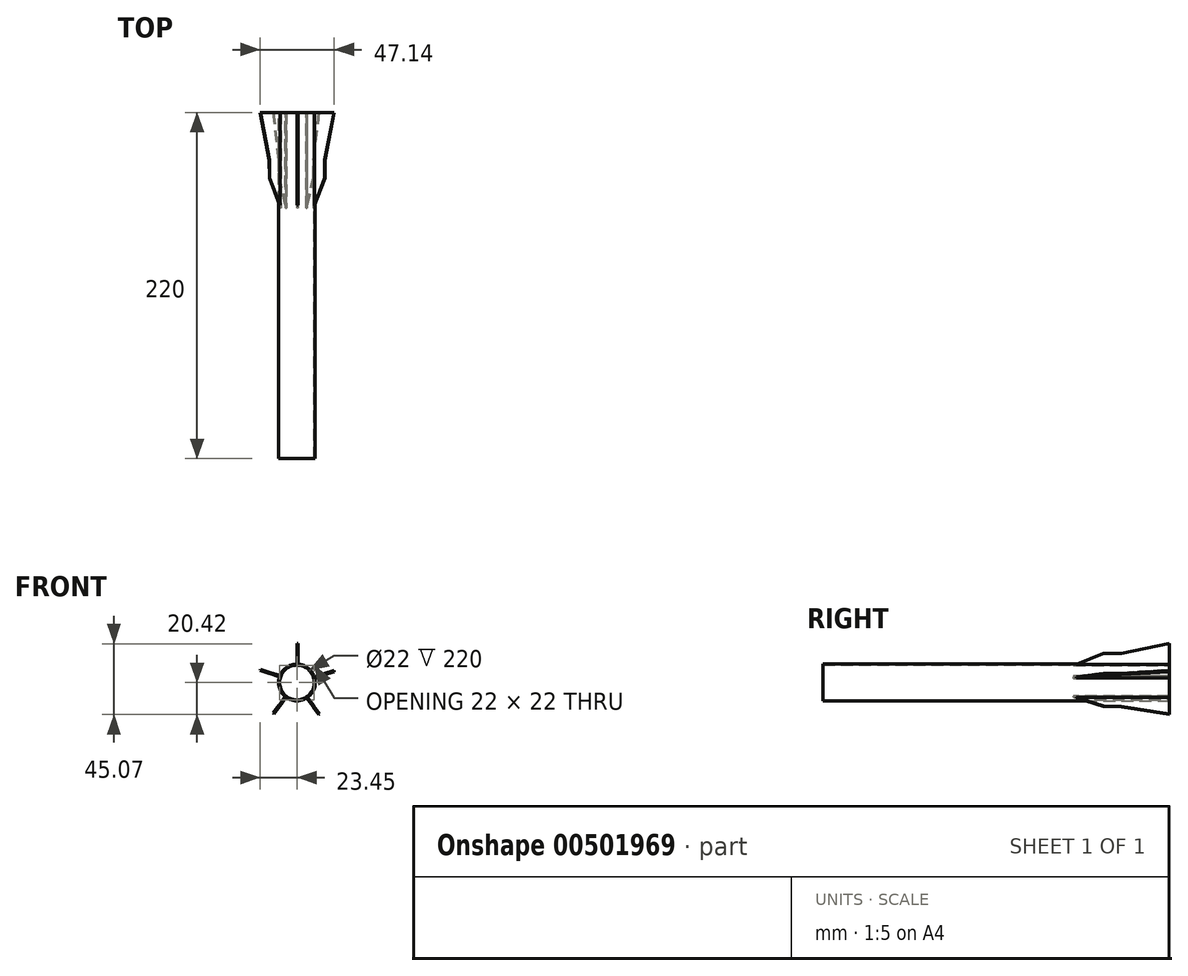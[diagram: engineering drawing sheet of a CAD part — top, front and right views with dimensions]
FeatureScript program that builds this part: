
annotation { "Feature Type Name" : "Feature", "Feature Type Description" : "" }
export const myFeature = defineFeature(function(context is Context, id is Id, definition is map)
    precondition{}
    {
        {
            var Q0;
            Q0=qCreatedBy(makeId("Front.planeOp"),FACE);
            var sketch = newSketch(context, id + "F0", { "sketchPlane" : qUnion([Q0])});
            skCircle(sketch, "E0", {"center": v(0, 0) * mm, "radius": 11 * mm});
            skCircle(sketch, "E1", {"center": v(0, 0) * mm, "radius": 11.65 * mm});
            skSolve(sketch);
        }
        {
            var Q0;
            Q0=makeQuery(id+"F0.imprint","IMPRINT",FACE,{"disambiguationData":[TD([[makeQuery(id+"F0.imprint","IMPRINT",EDGE,{"derivedFrom":sQuery(id+"F0.wireOp",EDGE,"E0")}),-1.0]])]});
            extrude(context, id + "F1", {"entities" : qUnion([Q0]), "depth" : 220 * mm});
        }
        {
            var Q0;
            Q0=qCreatedBy(makeId("Right.planeOp"),FACE);
            var sketch = newSketch(context, id + "F2", { "sketchPlane" : qUnion([Q0])});
            skLineSegment(sketch, "E2", {"start": v(0, 10.93) * mm, "end": v(-60.8, 10.93) * mm});
            skLineSegment(sketch, "E3", {"start": v(-60.8, 10.93) * mm, "end": v(-41.75, 18.38) * mm});
            skLineSegment(sketch, "E4", {"start": v(-41.75, 18.38) * mm, "end": v(-30.4, 18.6) * mm});
            skPoint(sketch, "E4.endSnap0", {"position": v(-30.4, 10.93) * mm});
            skLineSegment(sketch, "E5", {"start": v(-30.4, 18.6) * mm, "end": v(0, 24.65) * mm});
            skLineSegment(sketch, "E6", {"start": v(0, 24.65) * mm, "end": v(0, 10.93) * mm});
            skSolve(sketch);
        }
        {
            var Q0;
            Q0=makeQuery(id+"F2.imprint","IMPRINT",FACE,{"disambiguationData":[TD([[makeQuery(id+"F2.imprint","IMPRINT",EDGE,{"derivedFrom":sQuery(id+"F2.wireOp",EDGE,"E2")}),-1.0]])]});
            extrude(context, id + "F3", {"entities" : qUnion([Q0]), "operationType" : NewBodyOperationType.ADD, "depth" : 0.8 * mm});
        }
        {
            var Q0;
            Q0=makeQuery(id+"F1.opExtrude","SWEPT_BODY",BODY,{"disambiguationData":[OSD([sQuery(id+"F0.wireOp",EDGE,"E0")])]});
            var Q1;
            Q1=makeQuery(id+"F1.opExtrude","SWEPT_FACE",FACE,{"disambiguationData":[OSD([sQuery(id+"F0.wireOp",EDGE,"E0")])]});
            circularPattern(context, id + "F4", {"operationType" : NewBodyOperationType.ADD, "entities" : qUnion([Q0]), "axis" : qUnion([Q1]), "angle" : 360 * degree, "instanceCount" : 5, "oppositeDirection" : true, "equalSpace" : true});
        }
    });
